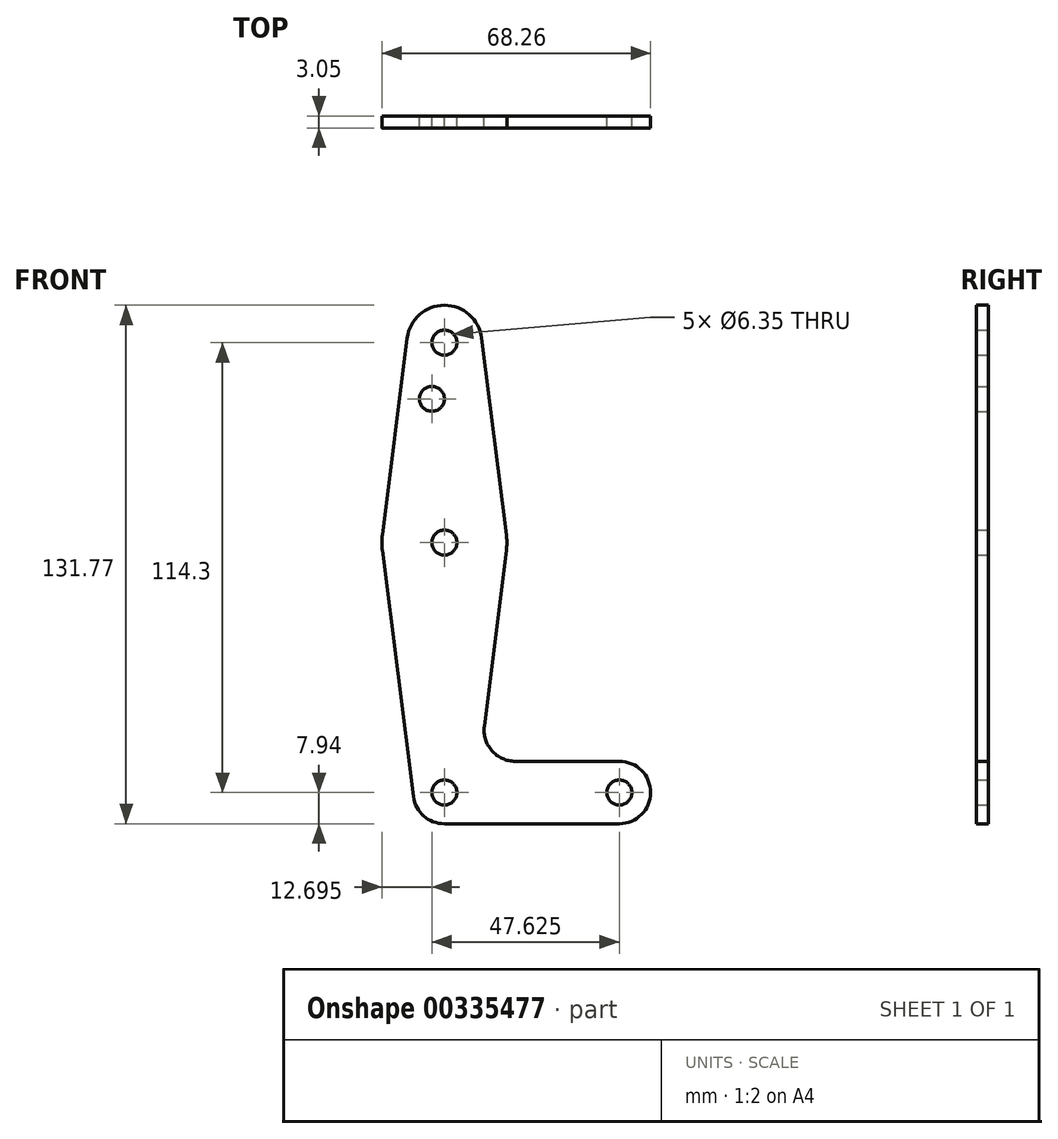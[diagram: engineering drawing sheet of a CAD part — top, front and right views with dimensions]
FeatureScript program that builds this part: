
annotation { "Feature Type Name" : "Feature", "Feature Type Description" : "" }
export const myFeature = defineFeature(function(context is Context, id is Id, definition is map)
    precondition{}
    {
        {
            var Q0;
            Q0=qCreatedBy(makeId("Front.planeOp"),FACE);
            var sketch = newSketch(context, id + "F0", { "sketchPlane" : qUnion([Q0])});
            skCircle(sketch, "E0", {"center": v(0, 0) * mm, "radius": 7.94 * mm});
            skLineSegment(sketch, "E1", {"start": v(0, 0) * mm, "end": v(44.45, 0) * mm, "construction": true});
            skCircle(sketch, "E2", {"center": v(44.45, 0) * mm, "radius": 7.94 * mm});
            skLineSegment(sketch, "E3", {"start": v(0, 0) * mm, "end": v(0, 63.5) * mm, "construction": true});
            skCircle(sketch, "E4", {"center": v(0, 63.5) * mm, "radius": 15.88 * mm});
            skLineSegment(sketch, "E5", {"start": v(0, 63.5) * mm, "end": v(0, 114.3) * mm, "construction": true});
            skCircle(sketch, "E6", {"center": v(0, 114.3) * mm, "radius": 9.53 * mm});
            skLineSegment(sketch, "E7", {"start": v(9.45, 115.5) * mm, "end": v(15.75, 65.48) * mm});
            skLineSegment(sketch, "E8", {"start": v(-9.45, 115.5) * mm, "end": v(-15.75, 65.48) * mm});
            skLineSegment(sketch, "E9", {"start": v(15.75, 61.52) * mm, "end": v(10.13, 16.88) * mm});
            skLineSegment(sketch, "E10", {"start": v(-7.88, -1) * mm, "end": v(-15.75, 61.52) * mm});
            skLineSegment(sketch, "E11", {"start": v(18.01, 7.94) * mm, "end": v(44.45, 7.94) * mm});
            skCircle(sketch, "E12", {"center": v(0, 114.3) * mm, "radius": 3.18 * mm});
            skCircle(sketch, "E13", {"center": v(0, 0) * mm, "radius": 3.18 * mm});
            skCircle(sketch, "E14", {"center": v(44.45, 0) * mm, "radius": 3.18 * mm});
            skCircle(sketch, "E15", {"center": v(0, 63.5) * mm, "radius": 3.18 * mm});
            skLineSegment(sketch, "E16", {"start": v(0, -7.94) * mm, "end": v(44.45, -7.94) * mm});
            skCircle(sketch, "E17", {"center": v(-3.18, 100.03) * mm, "radius": 3.18 * mm});
            skArc(sketch, "E18.filletArc", {"start": v(10.13, 16.88) * mm, "mid": v(12.05, 10.63) * mm, "end": v(18.01, 7.94) * mm});
            skSolve(sketch);
        }
        {
            var Q0;
            {var subQ0=sQuery(id+"F0.wireOp",EDGE,"2ZiuOdRH-vZkK-MRJk-ahbo-qATWZzzuUf2O");var subQ1=sQuery(id+"F0.wireOp",EDGE,"E0");var subQ2=makeQuery(id+"F0.imprint","INTERSECT",VERTEX,{"disambiguationData":[OD(0.0)],"derivedFrom":[subQ1,subQ0]});Q0=makeQuery(id+"F0.imprint","IMPRINT",FACE,{"disambiguationData":[TD([[makeQuery(id+"F0.imprint","IMPRINT",EDGE,{"disambiguationData":[TD([[subQ2,-1.0]])],"derivedFrom":subQ1}),1.0]])]});}
            var Q1;
            {var subQ0=sQuery(id+"F0.wireOp",EDGE,"E11");var subQ1=sQuery(id+"F0.wireOp",EDGE,"E0");var subQ3=makeQuery(id+"F0.imprint","INTERSECT",VERTEX,{"derivedFrom":[subQ1,subQ0]});Q1=makeQuery(id+"F0.imprint","IMPRINT",FACE,{"disambiguationData":[TD([[makeQuery(id+"F0.imprint","IMPRINT",EDGE,{"disambiguationData":[TD([[subQ3,-1.0]])],"derivedFrom":subQ1}),1.0]])]});}
            var Q2;
            {var subQ0=sQuery(id+"F0.wireOp",EDGE,"E9");var subQ1=sQuery(id+"F0.wireOp",EDGE,"E1");var subQ2=makeQuery(id+"F0.imprint","INTERSECT",VERTEX,{"derivedFrom":[subQ1,subQ0]});Q2=makeQuery(id+"F0.imprint","IMPRINT",FACE,{"disambiguationData":[TD([[makeQuery(id+"F0.imprint","IMPRINT",EDGE,{"disambiguationData":[TD([[subQ2,-1.0]])],"derivedFrom":subQ1}),1.0]])]});}
            var Q3;
            Q3=makeQuery(id+"F0.imprint","IMPRINT",FACE,{"disambiguationData":[TD([[makeQuery(id+"F0.imprint","IMPRINT",EDGE,{"derivedFrom":sQuery(id+"F0.wireOp",EDGE,"E14")}),-1.0]])]});
            var Q4;
            {var subQ0=sQuery(id+"F0.wireOp",EDGE,"E4");var subQ2=sQuery(id+"F0.wireOp",EDGE,"E3");var subQ3=makeQuery(id+"F0.imprint","INTERSECT",VERTEX,{"derivedFrom":[subQ2,subQ0]});Q4=makeQuery(id+"F0.imprint","IMPRINT",FACE,{"disambiguationData":[TD([[makeQuery(id+"F0.imprint","IMPRINT",EDGE,{"disambiguationData":[TD([[subQ3,-1.0]])],"derivedFrom":subQ2}),1.0]])]});}
            var Q5;
            {var subQ0=sQuery(id+"F0.wireOp",EDGE,"E7");Q5=makeQuery(id+"F0.imprint","IMPRINT",FACE,{"disambiguationData":[TD([[makeQuery(id+"F0.imprint","IMPRINT",EDGE,{"derivedFrom":subQ0}),-1.0]])]});}
            var Q6;
            {var subQ0=sQuery(id+"F0.wireOp",EDGE,"E8");Q6=makeQuery(id+"F0.imprint","IMPRINT",FACE,{"disambiguationData":[TD([[makeQuery(id+"F0.imprint","IMPRINT",EDGE,{"derivedFrom":subQ0}),1.0]])]});}
            var Q7;
            Q7=makeQuery(id+"F0.imprint","IMPRINT",FACE,{"disambiguationData":[TD([[makeQuery(id+"F0.imprint","IMPRINT",EDGE,{"derivedFrom":sQuery(id+"F0.wireOp",EDGE,"E12")}),-1.0]])]});
            var Q8;
            {var subQ0=sQuery(id+"F0.wireOp",EDGE,"E11");var subQ2=sQuery(id+"F0.wireOp",EDGE,"E0");var subQ4=makeQuery(id+"F0.imprint","INTERSECT",VERTEX,{"derivedFrom":[subQ2,subQ0]});Q8=makeQuery(id+"F0.imprint","IMPRINT",FACE,{"disambiguationData":[TD([[makeQuery(id+"F0.imprint","IMPRINT",EDGE,{"disambiguationData":[TD([[subQ4,1.0]])],"derivedFrom":subQ2}),1.0]])]});}
            var Q9;
            {var subQ0=sQuery(id+"F0.wireOp",EDGE,"E11");var subQ1=sQuery(id+"F0.wireOp",EDGE,"E0");var subQ2=makeQuery(id+"F0.imprint","INTERSECT",VERTEX,{"derivedFrom":[subQ1,subQ0]});Q9=makeQuery(id+"F0.imprint","IMPRINT",FACE,{"disambiguationData":[TD([[makeQuery(id+"F0.imprint","IMPRINT",EDGE,{"disambiguationData":[TD([[subQ2,1.0]])],"derivedFrom":subQ1}),-1.0]])]});}
            var Q10;
            {var subQ1=sQuery(id+"F0.wireOp",EDGE,"E0");var subQ5=makeQuery(id+"F0.imprint","IMPRINT",VERTEX,{"derivedFrom":subQ1});Q10=makeQuery(id+"F0.imprint","IMPRINT",FACE,{"disambiguationData":[TD([[makeQuery(id+"F0.imprint","IMPRINT",EDGE,{"disambiguationData":[TD([[subQ5,-1.0]])],"derivedFrom":subQ1}),1.0]])]});}
            var Q11;
            {var subQ0=sQuery(id+"F0.wireOp",EDGE,"2ZiuOdRH-vZkK-MRJk-ahbo-qATWZzzuUf2O");var subQ6=sQuery(id+"F0.wireOp",EDGE,"E0");var subQ8=makeQuery(id+"F0.imprint","INTERSECT",VERTEX,{"disambiguationData":[OD(1.0)],"derivedFrom":[subQ6,subQ0]});Q11=makeQuery(id+"F0.imprint","IMPRINT",FACE,{"disambiguationData":[TD([[makeQuery(id+"F0.imprint","IMPRINT",EDGE,{"disambiguationData":[TD([[subQ8,-1.0]])],"derivedFrom":subQ6}),-1.0]])]});}
            var Q12;
            {var subQ0=sQuery(id+"F0.wireOp",EDGE,"E4");var subQ5=sQuery(id+"F0.wireOp",EDGE,"E3");var subQ6=makeQuery(id+"F0.imprint","INTERSECT",VERTEX,{"derivedFrom":[subQ5,subQ0]});Q12=makeQuery(id+"F0.imprint","IMPRINT",FACE,{"disambiguationData":[TD([[makeQuery(id+"F0.imprint","IMPRINT",EDGE,{"disambiguationData":[TD([[subQ6,-1.0]])],"derivedFrom":subQ5}),-1.0]])]});}
            var Q13;
            {var subQ4=sQuery(id+"F0.wireOp",EDGE,"E4");var subQ6=sQuery(id+"F0.wireOp",EDGE,"E9");var subQ7=makeQuery(id+"F0.imprint","INTERSECT",VERTEX,{"derivedFrom":[subQ4,subQ6]});Q13=makeQuery(id+"F0.imprint","IMPRINT",FACE,{"disambiguationData":[TD([[makeQuery(id+"F0.imprint","IMPRINT",EDGE,{"disambiguationData":[TD([[subQ7,1.0]])],"derivedFrom":subQ4}),-1.0]])]});}
            var Q14;
            Q14=makeQuery(id+"F0.imprint","IMPRINT",FACE,{"disambiguationData":[TD([[makeQuery(id+"F0.imprint","IMPRINT",EDGE,{"derivedFrom":sQuery(id+"F0.wireOp",EDGE,"E15")}),-1.0]])]});
            extrude(context, id + "F1", {"entities" : qUnion([Q0, Q1, Q2, Q3, Q4, Q5, Q6, Q7, Q8, Q9, Q10, Q11, Q12, Q13, Q14]), "depth" : 3.05 * mm});
        }
    });
